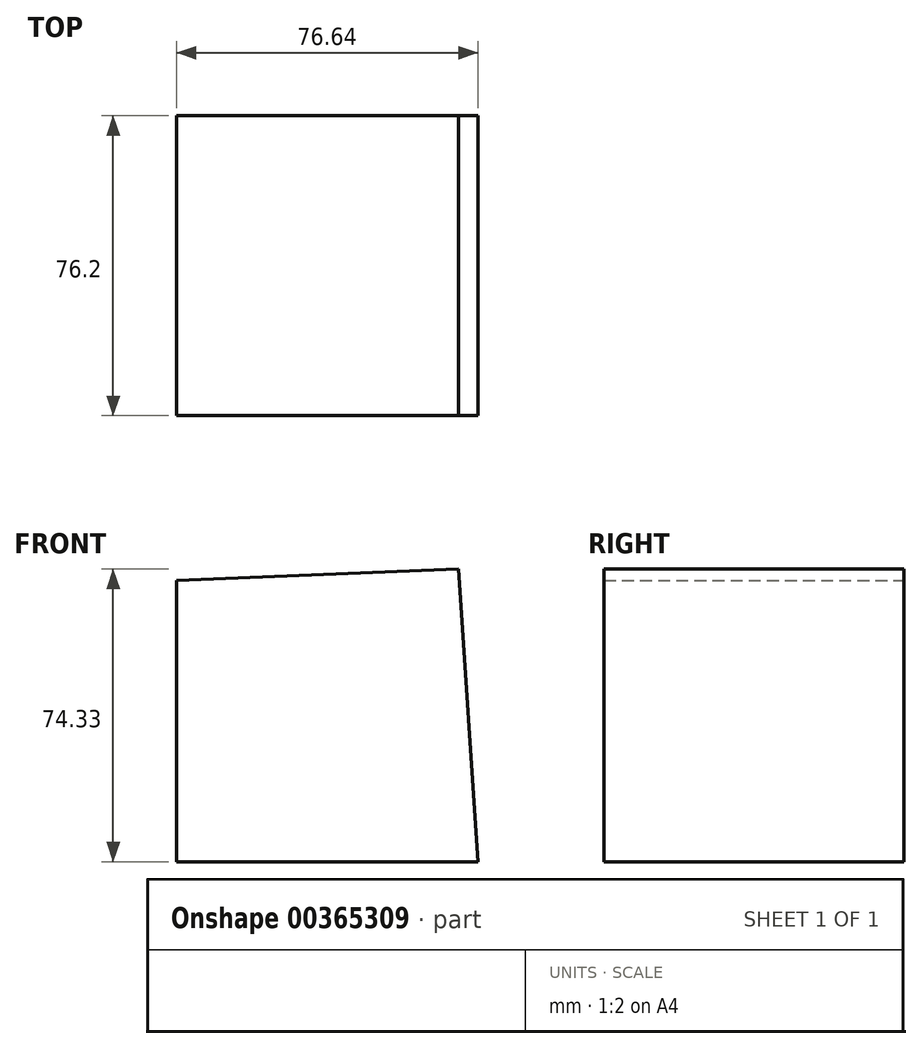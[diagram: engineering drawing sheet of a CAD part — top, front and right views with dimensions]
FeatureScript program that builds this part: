
annotation { "Feature Type Name" : "Feature", "Feature Type Description" : "" }
export const myFeature = defineFeature(function(context is Context, id is Id, definition is map)
    precondition{}
    {
        {
            var Q0;
            Q0=qCreatedBy(makeId("Front.planeOp"),FACE);
            var sketch = newSketch(context, id + "F0", { "sketchPlane" : qUnion([Q0])});
            skLineSegment(sketch, "E0", {"start": v(-43.33, 37.07) * mm, "end": v(-43.33, -34.37) * mm});
            skLineSegment(sketch, "E1", {"start": v(-43.33, -34.37) * mm, "end": v(33.31, -34.37) * mm});
            skLineSegment(sketch, "E2", {"start": v(33.31, -34.37) * mm, "end": v(28.3, 39.96) * mm});
            skLineSegment(sketch, "E3", {"start": v(28.3, 39.96) * mm, "end": v(-43.33, 37.07) * mm});
            skSolve(sketch);
        }
        {
            var Q0;
            Q0=makeQuery(id+"F0.imprint","IMPRINT",FACE,{"disambiguationData":[TD([[makeQuery(id+"F0.imprint","IMPRINT",EDGE,{"derivedFrom":sQuery(id+"F0.wireOp",EDGE,"E0")}),1.0]])]});
            extrude(context, id + "F1", {"entities" : qUnion([Q0]), "depth" : 76.2 * mm});
        }
    });
